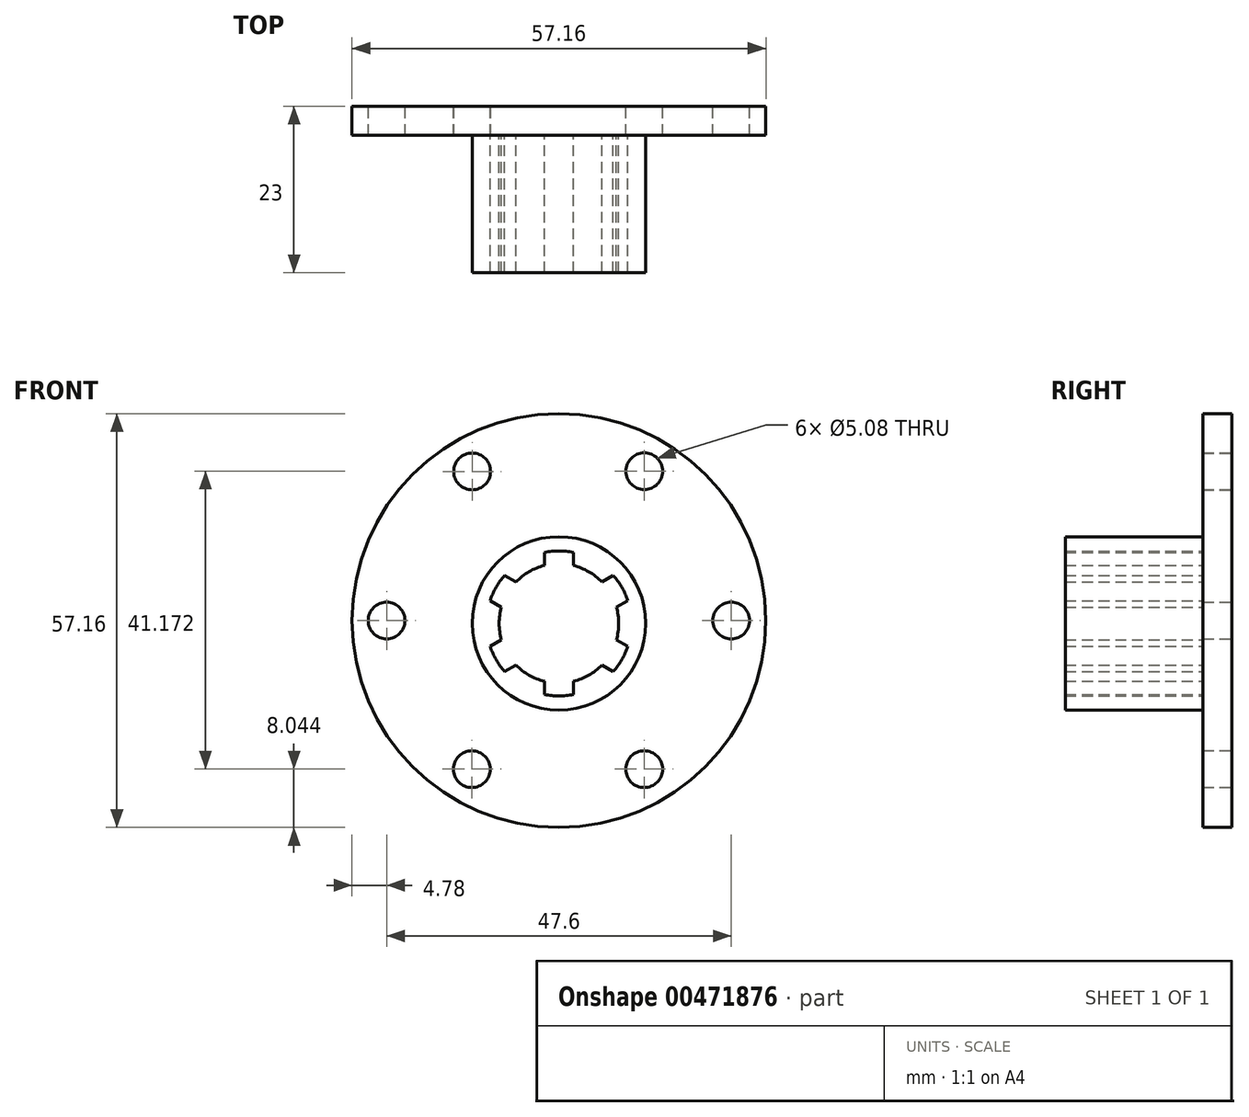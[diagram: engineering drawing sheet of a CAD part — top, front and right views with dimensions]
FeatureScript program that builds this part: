
annotation { "Feature Type Name" : "Feature", "Feature Type Description" : "" }
export const myFeature = defineFeature(function(context is Context, id is Id, definition is map)
    precondition{}
    {
        {
            var Q0;
            Q0=qCreatedBy(makeId("Front.planeOp"),FACE);
            var sketch = newSketch(context, id + "F0", { "sketchPlane" : qUnion([Q0])});
            skCircle(sketch, "E0", {"center": v(0, 0) * mm, "radius": 28.57 * mm});
            skCircle(sketch, "E1", {"center": v(0, 0) * mm, "radius": 23.8 * mm, "construction": true});
            skCircle(sketch, "E2", {"center": v(23.8, 0) * mm, "radius": 2.54 * mm});
            skCircle(sketch, "E3.MirrorC", {"center": v(-23.8, 0) * mm, "radius": 2.54 * mm});
            skLineSegment(sketch, "E4.0", {"start": v(-23.8, 0) * mm, "end": v(-11.9, 20.61) * mm, "construction": true});
            skLineSegment(sketch, "E4.1", {"start": v(-11.9, 20.61) * mm, "end": v(11.9, 20.61) * mm, "construction": true});
            skLineSegment(sketch, "E4.2", {"start": v(11.9, 20.61) * mm, "end": v(23.8, 0) * mm, "construction": true});
            skLineSegment(sketch, "E4.3", {"start": v(23.8, 0) * mm, "end": v(11.9, -20.61) * mm, "construction": true});
            skLineSegment(sketch, "E4.4", {"start": v(11.9, -20.61) * mm, "end": v(-11.9, -20.61) * mm, "construction": true});
            skLineSegment(sketch, "E4.5", {"start": v(-11.9, -20.61) * mm, "end": v(-23.8, 0) * mm, "construction": true});
            skCircle(sketch, "E5.MirrorC", {"center": v(-12.04, -20.54) * mm, "radius": 2.54 * mm});
            skCircle(sketch, "E6.MirrorC", {"center": v(11.77, -20.54) * mm, "radius": 2.54 * mm});
            skCircle(sketch, "E7.MirrorC", {"center": v(11.79, 20.64) * mm, "radius": 2.54 * mm});
            skCircle(sketch, "E8.MirrorC", {"center": v(-11.99, 20.6) * mm, "radius": 2.54 * mm});
            skSolve(sketch);
        }
        {
            var Q0;
            Q0=qCreatedBy(makeId("Front.planeOp"),FACE);
            var sketch = newSketch(context, id + "F1", { "sketchPlane" : qUnion([Q0])});
            skFitSpline(sketch, "E9.0.0", {"points": [v(-7.19, 95.35) * mm, v(-7.19, 95.95) * mm, v(-7.19, 96.55) * mm, v(-7.19, 97.15) * mm]});
            skArc(sketch, "E9.0.1", {"start": v(-7.19, 97.15) * mm, "mid": v(-9.2, 97.36) * mm, "end": v(-11.22, 97.15) * mm});
            skFitSpline(sketch, "E9.0.2", {"points": [v(-11.22, 97.15) * mm, v(-11.22, 96.55) * mm, v(-11.22, 95.95) * mm, v(-11.22, 95.35) * mm]});
            skArc(sketch, "E10.0", {"start": v(-11.22, 95.35) * mm, "mid": v(-13.33, 94.5) * mm, "end": v(-15.13, 93.09) * mm});
            skFitSpline(sketch, "E11.0.0", {"points": [v(-15.13, 93.09) * mm, v(-15.65, 93.4) * mm, v(-16.17, 93.7) * mm, v(-16.7, 94) * mm]});
            skArc(sketch, "E11.0.1", {"start": v(-16.7, 94) * mm, "mid": v(-17.88, 92.35) * mm, "end": v(-18.7, 90.5) * mm});
            skFitSpline(sketch, "E11.0.2", {"points": [v(-18.7, 90.5) * mm, v(-18.19, 90.2) * mm, v(-17.67, 89.9) * mm, v(-17.14, 89.6) * mm]});
            skArc(sketch, "E12.0", {"start": v(-17.14, 89.6) * mm, "mid": v(-17.46, 87.34) * mm, "end": v(-17.14, 85.08) * mm});
            skFitSpline(sketch, "E13.0.0", {"points": [v(-17.14, 85.08) * mm, v(-17.67, 84.78) * mm, v(-18.19, 84.48) * mm, v(-18.7, 84.18) * mm]});
            skArc(sketch, "E13.0.1", {"start": v(-18.7, 84.18) * mm, "mid": v(-17.88, 82.33) * mm, "end": v(-16.7, 80.7) * mm});
            skFitSpline(sketch, "E13.0.2", {"points": [v(-16.7, 80.7) * mm, v(-16.17, 81) * mm, v(-15.65, 81.3) * mm, v(-15.13, 81.6) * mm]});
            skArc(sketch, "E14.0", {"start": v(-15.13, 81.6) * mm, "mid": v(-13.33, 80.2) * mm, "end": v(-11.22, 79.33) * mm});
            skFitSpline(sketch, "E15.0.0", {"points": [v(-11.22, 79.33) * mm, v(-11.22, 78.73) * mm, v(-11.22, 78.13) * mm, v(-11.22, 77.53) * mm]});
            skArc(sketch, "E15.0.1", {"start": v(-11.22, 77.53) * mm, "mid": v(-9.2, 77.32) * mm, "end": v(-7.19, 77.53) * mm});
            skFitSpline(sketch, "E15.0.2", {"points": [v(-7.19, 77.53) * mm, v(-7.19, 78.13) * mm, v(-7.19, 78.73) * mm, v(-7.19, 79.33) * mm]});
            skArc(sketch, "E16.0", {"start": v(-7.19, 79.33) * mm, "mid": v(-5.07, 80.2) * mm, "end": v(-3.28, 81.6) * mm});
            skFitSpline(sketch, "E17.0.0", {"points": [v(-3.28, 81.6) * mm, v(-2.75, 81.3) * mm, v(-2.23, 81) * mm, v(-1.71, 80.7) * mm]});
            skArc(sketch, "E17.0.1", {"start": v(-1.71, 80.7) * mm, "mid": v(-0.53, 82.33) * mm, "end": v(0.3, 84.18) * mm});
            skFitSpline(sketch, "E17.0.2", {"points": [v(0.3, 84.18) * mm, v(-0.22, 84.48) * mm, v(-0.74, 84.78) * mm, v(-1.26, 85.08) * mm]});
            skFitSpline(sketch, "E18.0.0", {"points": [v(-1.26, 89.6) * mm, v(-0.74, 89.9) * mm, v(-0.22, 90.2) * mm, v(0.3, 90.5) * mm]});
            skArc(sketch, "E18.0.1", {"start": v(0.3, 90.5) * mm, "mid": v(-0.53, 92.35) * mm, "end": v(-1.71, 94) * mm});
            skFitSpline(sketch, "E18.0.2", {"points": [v(-1.71, 94) * mm, v(-2.23, 93.7) * mm, v(-2.75, 93.4) * mm, v(-3.28, 93.09) * mm]});
            skArc(sketch, "E19.0", {"start": v(-1.26, 85.08) * mm, "mid": v(-0.95, 87.34) * mm, "end": v(-1.26, 89.6) * mm});
            skArc(sketch, "E19.1", {"start": v(-3.28, 93.09) * mm, "mid": v(-5.07, 94.5) * mm, "end": v(-7.19, 95.35) * mm});
            skCircle(sketch, "E20.0", {"center": v(-9.2, 87.34) * mm, "radius": 11.98 * mm});
            skFitSpline(sketch, "E21.0.0", {"points": [v(2.01, 7.6) * mm, v(2.01, 8.21) * mm, v(2.01, 8.81) * mm, v(2.01, 9.42) * mm]});
            skArc(sketch, "E21.0.1", {"start": v(2.01, 9.42) * mm, "mid": v(0, 9.62) * mm, "end": v(-2.02, 9.42) * mm});
            skFitSpline(sketch, "E21.0.2", {"points": [v(-2.02, 9.42) * mm, v(-2.02, 8.81) * mm, v(-2.02, 8.21) * mm, v(-2.02, 7.6) * mm]});
            skArc(sketch, "E22.0", {"start": v(-2.02, 7.6) * mm, "mid": v(-4.13, 6.75) * mm, "end": v(-5.93, 5.35) * mm});
            skFitSpline(sketch, "E23.0.0", {"points": [v(-5.93, 5.35) * mm, v(-6.45, 5.65) * mm, v(-6.97, 5.95) * mm, v(-7.5, 6.25) * mm]});
            skArc(sketch, "E23.0.1", {"start": v(-7.5, 6.25) * mm, "mid": v(-8.68, 4.61) * mm, "end": v(-9.5, 2.77) * mm});
            skFitSpline(sketch, "E23.0.2", {"points": [v(-9.5, 2.77) * mm, v(-8.99, 2.47) * mm, v(-8.47, 2.16) * mm, v(-7.94, 1.86) * mm]});
            skArc(sketch, "E24.0", {"start": v(-7.94, 1.86) * mm, "mid": v(-8.26, -0.4) * mm, "end": v(-7.94, -2.66) * mm});
            skFitSpline(sketch, "E25.0.0", {"points": [v(-7.94, -2.66) * mm, v(-8.47, -2.96) * mm, v(-8.99, -3.26) * mm, v(-9.5, -3.56) * mm]});
            skArc(sketch, "E25.0.1", {"start": v(-9.5, -3.56) * mm, "mid": v(-8.68, -5.4) * mm, "end": v(-7.5, -7.05) * mm});
            skFitSpline(sketch, "E25.0.2", {"points": [v(-7.5, -7.05) * mm, v(-6.97, -6.75) * mm, v(-6.45, -6.45) * mm, v(-5.93, -6.14) * mm]});
            skArc(sketch, "E26.0", {"start": v(-5.93, -6.14) * mm, "mid": v(-4.13, -7.55) * mm, "end": v(-2.02, -8.4) * mm});
            skFitSpline(sketch, "E27.0.0", {"points": [v(-2.02, -8.4) * mm, v(-2.02, -9) * mm, v(-2.02, -9.6) * mm, v(-2.02, -10.21) * mm]});
            skArc(sketch, "E27.0.1", {"start": v(-2.02, -10.21) * mm, "mid": v(0, -10.41) * mm, "end": v(2.01, -10.21) * mm});
            skFitSpline(sketch, "E27.0.2", {"points": [v(2.01, -10.21) * mm, v(2.01, -9.6) * mm, v(2.01, -9) * mm, v(2.01, -8.4) * mm]});
            skArc(sketch, "E28.0", {"start": v(2.01, -8.4) * mm, "mid": v(4.13, -7.55) * mm, "end": v(5.93, -6.14) * mm});
            skFitSpline(sketch, "E29.0.0", {"points": [v(5.93, -6.14) * mm, v(6.45, -6.45) * mm, v(6.97, -6.75) * mm, v(7.49, -7.05) * mm]});
            skArc(sketch, "E29.0.1", {"start": v(7.49, -7.05) * mm, "mid": v(8.67, -5.4) * mm, "end": v(9.5, -3.56) * mm});
            skFitSpline(sketch, "E29.0.2", {"points": [v(9.5, -3.56) * mm, v(8.98, -3.26) * mm, v(8.46, -2.96) * mm, v(7.94, -2.66) * mm]});
            skFitSpline(sketch, "E30.0.0", {"points": [v(7.94, 1.86) * mm, v(8.46, 2.16) * mm, v(8.98, 2.47) * mm, v(9.5, 2.77) * mm]});
            skArc(sketch, "E30.0.1", {"start": v(9.5, 2.77) * mm, "mid": v(8.67, 4.61) * mm, "end": v(7.49, 6.25) * mm});
            skFitSpline(sketch, "E30.0.2", {"points": [v(7.49, 6.25) * mm, v(6.97, 5.95) * mm, v(6.45, 5.65) * mm, v(5.93, 5.35) * mm]});
            skArc(sketch, "E31.0", {"start": v(7.94, -2.66) * mm, "mid": v(8.25, -0.4) * mm, "end": v(7.94, 1.86) * mm});
            skArc(sketch, "E31.1", {"start": v(5.93, 5.35) * mm, "mid": v(4.13, 6.75) * mm, "end": v(2.01, 7.6) * mm});
            skCircle(sketch, "E32.0", {"center": v(0, -0.4) * mm, "radius": 11.98 * mm});
            skSolve(sketch);
        }
        {
            var Q0;
            Q0=makeQuery(id+"F1.imprint","IMPRINT",FACE,{"disambiguationData":[TD([[makeQuery(id+"F1.imprint","IMPRINT",EDGE,{"derivedFrom":sQuery(id+"F1.wireOp",EDGE,"E21.0.0")}),-1.0]])]});
            extrude(context, id + "F2", {"entities" : qUnion([Q0]), "depth" : 23 * mm});
        }
        {
            var Q0;
            Q0=makeQuery(id+"F0.imprint","IMPRINT",FACE,{"disambiguationData":[TD([[makeQuery(id+"F0.imprint","IMPRINT",EDGE,{"derivedFrom":sQuery(id+"F0.wireOp",EDGE,"E0")}),1.0]])]});
            extrude(context, id + "F3", {"entities" : qUnion([Q0]), "operationType" : NewBodyOperationType.ADD, "depth" : 4 * mm});
        }
    });
